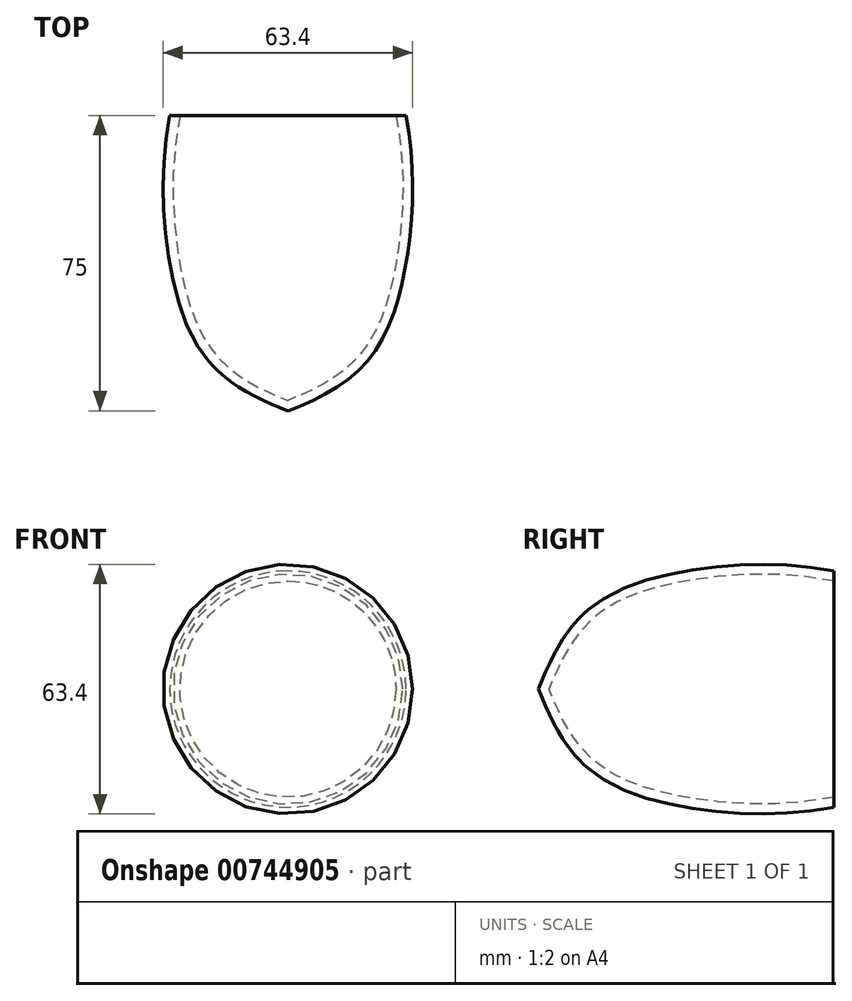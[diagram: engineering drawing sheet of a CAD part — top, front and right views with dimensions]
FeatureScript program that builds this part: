
annotation { "Feature Type Name" : "Feature", "Feature Type Description" : "" }
export const myFeature = defineFeature(function(context is Context, id is Id, definition is map)
    precondition{}
    {
        {
            var Q0;
            Q0=qCreatedBy(makeId("Top.planeOp"),FACE);
            var sketch = newSketch(context, id + "F0", { "sketchPlane" : qUnion([Q0])});
            skLineSegment(sketch, "E0", {"start": v(0, -27.38) * mm, "end": v(0, 0) * mm});
            skLineSegment(sketch, "E1", {"start": v(0, -27.38) * mm, "end": v(0, -102.38) * mm});
            skLineSegment(sketch, "E2", {"start": v(0, -27.38) * mm, "end": v(30, -27.38) * mm});
            skFitSpline(sketch, "E3", {"points": [v(30, -27.38) * mm, v(30, -64.95) * mm, v(19.98, -90.01) * mm, v(0, -102.38) * mm], "startDerivative": vector(19.84, -102) * mm, "endDerivative": vector(-73.6, -27.43) * mm});
            skLineSegment(sketch, "E4", {"start": v(0, -102.38) * mm, "end": v(0, -167.38) * mm});
            skLineSegment(sketch, "E5", {"start": v(0, -167.38) * mm, "end": v(-3, -167.38) * mm});
            skLineSegment(sketch, "E6", {"start": v(-3, -167.38) * mm, "end": v(-3, -102.38) * mm});
            skLineSegment(sketch, "E7", {"start": v(0, -102.38) * mm, "end": v(-3, -102.38) * mm});
            skSolve(sketch);
        }
        {
            var Q0;
            {var subQ0=sQuery(id+"F0.wireOp",EDGE,"E2");Q0=makeQuery(id+"F0.imprint","IMPRINT",FACE,{"disambiguationData":[TD([[makeQuery(id+"F0.imprint","IMPRINT",EDGE,{"derivedFrom":subQ0}),-1.0]])]});}
            var Q1;
            Q1=sQuery(id+"F0.wireOp",EDGE,"E1");
            revolve(context, id + "F1", {"surfaceOperationType" : NewSurfaceOperationType.NEW, "entities" : qUnion([Q0]), "axis" : qUnion([Q1]), "revolveType" : RevolveType.FULL});
        }
        {
            var Q0;
            Q0=makeQuery(id+"F1.opRevolve","SWEPT_FACE",FACE,{"disambiguationData":[OSD([sQuery(id+"F0.wireOp",EDGE,"E2")])]});
            shell(context, id + "F2", {"entities" : qUnion([Q0]), "thickness" : 2.5 * mm});
        }
    });
